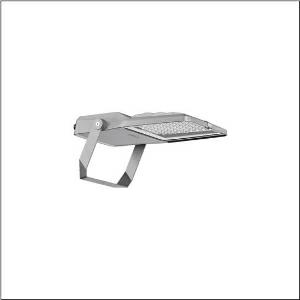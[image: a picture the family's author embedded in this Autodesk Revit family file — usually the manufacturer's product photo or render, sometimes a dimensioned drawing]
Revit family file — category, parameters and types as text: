
# Revit family: floodlight_fl_21_iq_mini___pl64_5xa7772b3e1a_f8e6
name_source: partatom
category: Lighting Fixtures
units: mm (PartAtom-declared; Revit-internal decimal feet)

## family parameters
Cut with Voids When Loaded = No
Host = Face
Light Source = No
Part Type = Normal
Room Calculation Point = No
Round Connector Dimension = Use Diameter
Shared = No

## types (1)
- --- (1 x LED, 5190 lm, 45.5 W, 3000K)
    Apparent Load = 46 VA
    CIE Flux Codes = 28 80 98 100 100
    Color Rendering = 80
    Color Temperature = 3000K
    Default Elevation = 1800 mm
    Description = Floodlight FL 21 iQ mini, floodlight, primary light control with lens, of PMMA, primary optical cover: protective disc, of toughened safety glass, transparent, light distribution: PL64, light emission: direct distribution, installation type: surface-mounted, LED, High Power LED, rated luminous flux: 5.190lm, luminous efficacy: 114lm/W, light colour: 830, colour temperature: 3000K, control gear: iQ Street-Remote/DALI, control: Street-Remote, Auto-Match, Temp-Guard, Night-Set, Smart-Wire, Desk-Remote (wireless, voltage-free reading and setting of iQ features in the workshop via application-optimized NFC function/RFID function), optimised constant luminous flux control (CLO 2.0), with terminal, 6-pole, mains connection: 220..240V, AC, 50/60Hz, start of lifetime: 46W, end of service life: 48W, reduction: 21W, luminaire housing, of diecast aluminium, powder-coated, Siteco® metallic grey (DB 702S), corrosivity category C5 mid according to DIN EN ISO 12944, suitable for swimming pools, chlorine-resistant, sealing non-destructively replaceable, mounting bracket, of steel, galvanised, powder-coated, Siteco® metallic grey (DB 702S), protection rating (complete): IP66, insulation class (complete): insulation class II (safety insulation), certification: CE, ENEC, VDE, protection symbol: D, impact resistance: IK08, permissible operating ambient temperature: -40..+40°C, permissible operating ambient temperature for outdoor applications: -40..+50°C, standard: DIN EN 12944, LABS conformity tested according to VDMA 24364:2018-05, packaging unit: 1 piece

Light Distribution: PL64
    Height = 70 mm
    Lamp = 1 x LED
    Lamp Light Flux = 5190 lm
    Lamp Power = 45.5 W
    Lamp count = 1
    Length = 485 mm
    Luminous efficacy = 114 lm/W
    Manufacturer = Siteco
    ModVariant = No
    Model = 5XA7772B3E1A
    Number of Poles = 1
    OnlyDefault = Yes
    Power Factor = 1
    Product Name = Floodlight FL 21 iQ mini | PL64
    Product group = floodlight | pylon annexe
    ProductGroupID = 6200
    Protection Class = Protection class II
    Protection Degree = IP 66
    RLX_Detail_Level = 1
    RLX_Emergency_Light_Flux = 0 lm
    RLX_Emergency_Type = 0
    RLX_Emergency_Type_DB = No
    RlxData = <blob elided: 96129 chars, md5=cab643b8>
    Socket = socket
    Standby Power = 0 W
    System Light Flux = 5190 lm
    System Power = 46 W
    Type Comments = factory setting: luminous flux: 100 % | dim-lin: 254 | 463 mA
    Type Image = l_1006845.jpg
    URL = http://relux.com
    VarID = @adj_166866
    Voltage = 0 V
    Weight = 0.00 kg
    Width = 337 mm

## geometry (parser evidence)
native form markers: Blend x4, Sweep x13
no freeform markers — native parametric forms only
